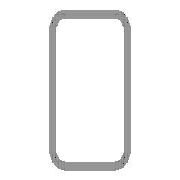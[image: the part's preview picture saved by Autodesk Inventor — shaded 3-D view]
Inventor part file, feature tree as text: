
AUTODESK INVENTOR PART (.ipt)
format: ipt  version: 2025.1 (Build 291241020, 241B)  size: 142,848 bytes
history: native  units: mm (DEFAULTED — no unit token found)
features: other x4, plane x2, split x1, sketch x1
ambient origin geometry x8: Origin, YZ Plane, XZ Plane, XY Plane, X Axis, Y Axis, Z Axis, Center Point
bodies: Solid1 (feature_tree), Body (feature_tree)
feature tree (8):
  parser-record x1  (decoder bookkeeping rows leaked as tree rows — omitted from the tree; the rows remain in map.json)
  other  "Driven Length"
  other  "Start Plane"
  other  "End Plane"
  plane  "Work Plane4"
  split  "Split1"
  sketch  "Sketch3"  dims[d3=404.948996mm d4=0.0mm d7=6.0mm d9=40.0mm d11=80.0mm d12=3.0mm d13=80.0mm d14=484.948996mm d15=20.0mm d16=40.0mm d17=90.0deg d18=404.948996mm]
  plane  "Work Plane3"
